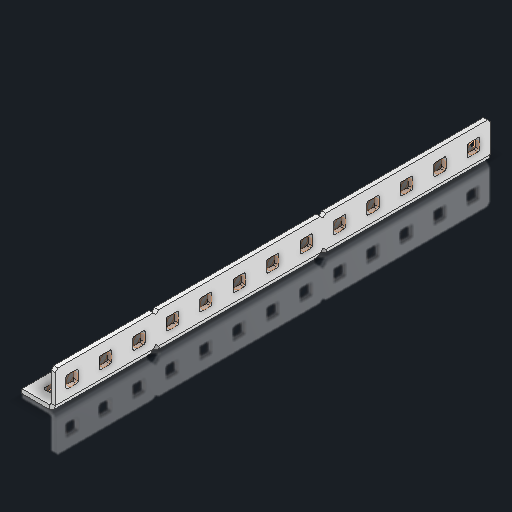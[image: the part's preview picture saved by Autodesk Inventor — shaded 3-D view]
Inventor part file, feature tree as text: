
AUTODESK INVENTOR PART (.ipt)
format: ipt  version: 2023.2 (Build 272271030, 271C)  size: 584,704 bytes
history: native  units: in
note: dims shown in document units (in); Inventor stores cm internally (conversion verified against a paired STEP export)
features: other x58, sketch x8, sheet_metal_op x1
ambient origin geometry x8: Origin, YZ Plane, XZ Plane, XY Plane, X Axis, Y Axis, Z Axis, Center Point
bodies: Solid1 (feature_tree)
feature tree (67):
  other  "Alu C Half 1x3x1x13.ipt"
  other  "Solid1::Alu C Half 1x3x1x13.ipt"
  other  "TaggingFeature1"
  sketch  "Sketch1"  dims[d0=0.3937in]
  sketch  "Sketch2"  dims[d1=0.0625in]
  sketch  "Sketch3"
  sketch  "Sketch7"
  other  "Flange Pattern Sketch"
  sketch  "Sketch8"
  sketch  "Sketch9"
  sheet_metal_op  "Body Pattern Sketch"
  other  "Arc Length"
  sketch  "Sketch13"
  sketch  "Sketch14"
  other  "Flange Pattern Plane"
  other  "Srf1"
  other  "Srf2"
  other  "Srf3"
  other  "Srf4"
  other  "Srf5"
  other  "Srf6"
  other  "Srf7"
  other  "Srf8"
  other  "Srf9"
  other  "Srf10"
  other  "Srf11"
  other  "Srf12"
  other  "Srf13"
  other  "Srf14"
  other  "Srf15"
  other  "Srf16"
  other  "Srf17"
  other  "Srf18"
  other  "Srf19"
  other  "Srf20"
  other  "Srf21"
  other  "Srf22"
  other  "Srf23"
  other  "Srf24"
  other  "Srf25"
  other  "Srf26"
  other  "Srf1::Derived"
  other  "Srf2::Derived"
  other  "Srf1310::Derived"
  other  "Srf1311::Derived"
  other  "Srf1312::Derived"
  other  "Srf1728::Derived"
  other  "Srf1878::Derived"
  other  "Srf1879::Derived"
  other  "Srf1880::Derived"
  other  "Srf1881::Derived"
  other  "Srf1882::Derived"
  other  "Srf1883::Derived"
  other  "Srf1884::Derived"
  other  "Srf91::Derived"
  other  "Srf92::Derived"
  other  "Srf856::Derived"
  other  "Srf1376::Derived"
  other  "Srf1377::Derived"
  other  "Srf1755::Derived"
  other  "Srf1942::Derived"
  other  "Srf1943::Derived"
  other  "Srf1944::Derived"
  other  "Srf1945::Derived"
  other  "Srf1946::Derived"
  other  "Srf1947::Derived"
  other  "Srf1948::Derived"
